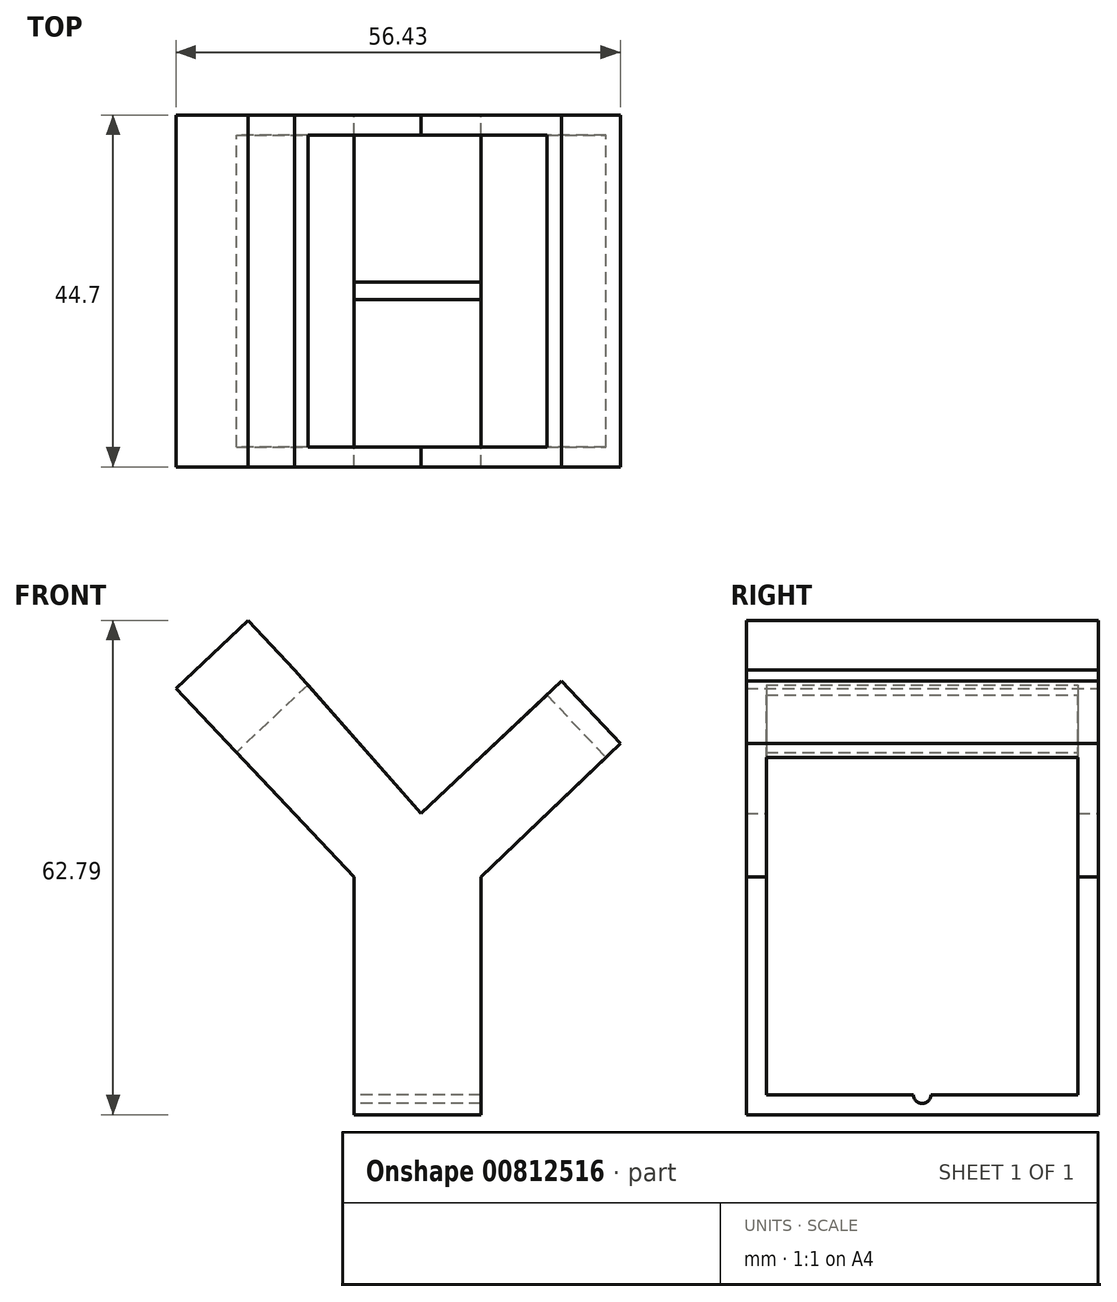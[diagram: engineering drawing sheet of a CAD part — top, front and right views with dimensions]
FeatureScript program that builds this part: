
annotation { "Feature Type Name" : "Feature", "Feature Type Description" : "" }
export const myFeature = defineFeature(function(context is Context, id is Id, definition is map)
    precondition{}
    {
        {
            var Q0;
            Q0=qCreatedBy(makeId("Front.planeOp"),FACE);
            var sketch = newSketch(context, id + "F0", { "sketchPlane" : qUnion([Q0])});
            skLineSegment(sketch, "E0", {"start": v(-103.72, 61.2) * mm, "end": v(-112.85, 52.57) * mm});
            skLineSegment(sketch, "E1", {"start": v(-112.85, 52.57) * mm, "end": v(-96.15, 34.89) * mm});
            skLineSegment(sketch, "E2", {"start": v(-96.15, 34.89) * mm, "end": v(-87.64, 42.93) * mm});
            skLineSegment(sketch, "E3", {"start": v(-87.64, 42.93) * mm, "end": v(-80.04, 34.89) * mm});
            skLineSegment(sketch, "E4", {"start": v(-80.04, 34.89) * mm, "end": v(-96.15, 34.89) * mm});
            skLineSegment(sketch, "E5", {"start": v(-87.64, 42.93) * mm, "end": v(-69.83, 59.75) * mm});
            skLineSegment(sketch, "E6", {"start": v(-69.83, 59.75) * mm, "end": v(-62.35, 51.83) * mm});
            skLineSegment(sketch, "E7", {"start": v(-62.35, 51.83) * mm, "end": v(-80.04, 34.89) * mm});
            skLineSegment(sketch, "E8", {"start": v(-96.15, 34.89) * mm, "end": v(-96.15, 4.69) * mm});
            skLineSegment(sketch, "E9", {"start": v(-96.15, 4.69) * mm, "end": v(-80.04, 4.69) * mm});
            skLineSegment(sketch, "E10", {"start": v(-80.04, 4.69) * mm, "end": v(-80.04, 34.89) * mm});
            skLineSegment(sketch, "E11", {"start": v(-103.72, 61.2) * mm, "end": v(-87.64, 42.93) * mm});
            skSolve(sketch);
        }
        {
            var Q0;
            Q0 = qSketchRegion(id + "F0", true);
            var Q1;
            Q1=makeQuery(id+"F0.imprint","IMPRINT",FACE,{"disambiguationData":[TD([[makeQuery(id+"F0.imprint","IMPRINT",EDGE,{"derivedFrom":sQuery(id+"F0.wireOp",EDGE,"E0")}),1.0]])]});
            extrude(context, id + "F1", {"entities" : qUnion([Q0, Q1]), "depth" : 44.7 * mm, "offsetDistance" : 25.4 * mm});
        }
        {
            var Q0;
            Q0=makeQuery(id+"F1.opExtrude","SWEPT_FACE",FACE,{"disambiguationData":[OSD([sQuery(id+"F0.wireOp",EDGE,"E1")])]});
            var Q1;
            Q1=makeQuery(id+"F1.opExtrude","SWEPT_FACE",FACE,{"disambiguationData":[OSD([sQuery(id+"F0.wireOp",EDGE,"E8")])]});
            var Q2;
            Q2=makeQuery(id+"F1.opExtrude","SWEPT_FACE",FACE,{"disambiguationData":[OSD([sQuery(id+"F0.wireOp",EDGE,"E10")])]});
            var Q3;
            Q3=makeQuery(id+"F1.opExtrude","SWEPT_FACE",FACE,{"disambiguationData":[OSD([sQuery(id+"F0.wireOp",EDGE,"E7")])]});
            var Q4;
            Q4=makeQuery(id+"F1.opExtrude","SWEPT_FACE",FACE,{"disambiguationData":[OSD([sQuery(id+"F0.wireOp",EDGE,"E11")])]});
            var Q5;
            Q5=makeQuery(id+"F1.opExtrude","SWEPT_FACE",FACE,{"disambiguationData":[OSD([sQuery(id+"F0.wireOp",EDGE,"E5")])]});
            shell(context, id + "F2", {"entities" : qUnion([Q0, Q1, Q2, Q3, Q4, Q5]), "thickness" : 2.54 * mm});
        }
        {
            var Q0;
            Q0=makeQuery(id+"F1.opExtrude","SWEPT_FACE",FACE,{"disambiguationData":[OSD([sQuery(id+"F0.wireOp",EDGE,"E0")])]});
            extrude(context, id + "F3", {"entities" : qUnion([Q0]), "operationType" : NewBodyOperationType.ADD, "depth" : 8.64 * mm, "offsetDistance" : 25.4 * mm});
        }
        {
            var Q0;
            Q0=makeQuery(id+"F1.opExtrude","SWEPT_FACE",FACE,{"disambiguationData":[OSD([sQuery(id+"F0.wireOp",EDGE,"E8")])]});
            var sketch = newSketch(context, id + "F4", { "sketchPlane" : qUnion([Q0])});
            skCircle(sketch, "E12", {"center": v(22.35, 7.23) * mm, "radius": 1.1 * mm});
            skSolve(sketch);
        }
        {
            var Q0;
            {var subQ0=sQuery(id+"F4.wireOp",EDGE,"E12");var subQ1=makeQuery(id+"F2.opShell","OFFSET_EDGE",EDGE,{"disambiguationData":[OSD([sQuery(id+"F0.wireOp",EDGE,"E8"),sQuery(id+"F0.wireOp",EDGE,"E9")])]});var subQ2=makeQuery(id+"F4.imprint","INTERSECT",VERTEX,{"disambiguationData":[OD(0.0)],"derivedFrom":[subQ1,subQ0]});Q0=makeQuery(id+"F4.imprint","IMPRINT",FACE,{"disambiguationData":[TD([[makeQuery(id+"F4.imprint","IMPRINT",EDGE,{"disambiguationData":[TD([[subQ2,-1.0]])],"derivedFrom":subQ0}),1.0]])]});}
            extrude(context, id + "F5", {"entities" : qUnion([Q0]), "operationType" : NewBodyOperationType.REMOVE, "oppositeDirection" : true, "depth" : 25.4 * mm, "offsetDistance" : 25.4 * mm});
        }
    });
